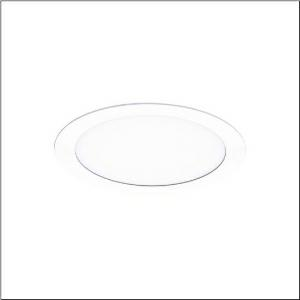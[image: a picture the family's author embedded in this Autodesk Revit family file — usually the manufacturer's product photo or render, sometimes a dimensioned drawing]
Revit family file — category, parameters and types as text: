
# Revit family: lunis_21_xl_51db16ef91c
name_source: partatom
category: Lighting Fixtures
units: mm (PartAtom-declared; Revit-internal decimal feet)

## family parameters
Cut with Voids When Loaded = No
Host = Face
Light Source = No
Part Type = Normal
Room Calculation Point = No
Round Connector Dimension = Use Diameter
Shared = No

## types (1)
- --- (1 x LED, 3300 lm, 25.4 W, 6500K)
    Apparent Load = 25 VA
    CIE Flux Codes = 50 80 96 100 100
    Color Rendering = 80
    Color Temperature = 6500K
    Default Elevation = 1800 mm
    Description = Lunis 21,  XL, downlight, light control with lens, of PMMA, optical cover: cover panel, of PC, opal, light emission: direct distribution, LED rated luminous flux: 1.960lm, light colour: 830/840/865, with terminal, 5-pole, mains connection: 220..240V, AC/DC, 0/50..60Hz, housing, round, of diecast aluminium, traffic white (RAL 9016), diameter: 230mm, clamping range: 1..40mm, protection rating (complete): IP20, protection rating (on room side): IP54, insulation class (complete): insulation class II (safety insulation), certification: CE, impact resistance: IK03, packaging unit: 1 piece
    Height = 0 mm  [stored 0 ft]
    Lamp = 1 x LED
    Lamp Light Flux = 3300 lm
    Lamp Power = 25.4 W
    Lamp count = 1
    Length = 230 mm
    Luminous efficacy = 130 lm/W
    Manufacturer = Siteco
    ModVariant = No
    Model = 51DB16EF91C
    Mounting Place = Ceiling
    Mounting Type = Recessed
    Number of Poles = 1
    OnlyDefault = Yes
    Power Factor = 1
    Product Name = Lunis 21 XL
    Product group = downlight
    ProductGroupID = 400
    Protection Class = Protection class II
    Protection Degree = IP 20
    RLX_Detail_Level = 1
    RLX_Emergency_Light_Flux = 0 lm
    RLX_Emergency_Type = 0
    RLX_Emergency_Type_DB = No
    RlxData = <blob elided: 18669 chars, md5=8628b766>
    Socket = socket
    Standby Power = 0 W
    System Light Flux = 3300 lm
    System Power = 25 W
    Type Comments = individual setting: colour temperature 6500K, luminous flux: 100 % | (ON | ON | OFF | OFF) | 700 mA
    Type Image = l_1291153.jpg
    URL = http://relux.com
    VarID = @adj_020808
    Voltage = 0 V
    Weight = 0.00 kg
    Width = 0 mm  [stored 0 ft]

note: [stored X ft] marks values corroborated as IEEE doubles in the binary element streams (Revit-internal decimal feet)

## geometry (parser evidence)
native form markers: Blend x4, Sweep x11
no freeform markers — native parametric forms only
